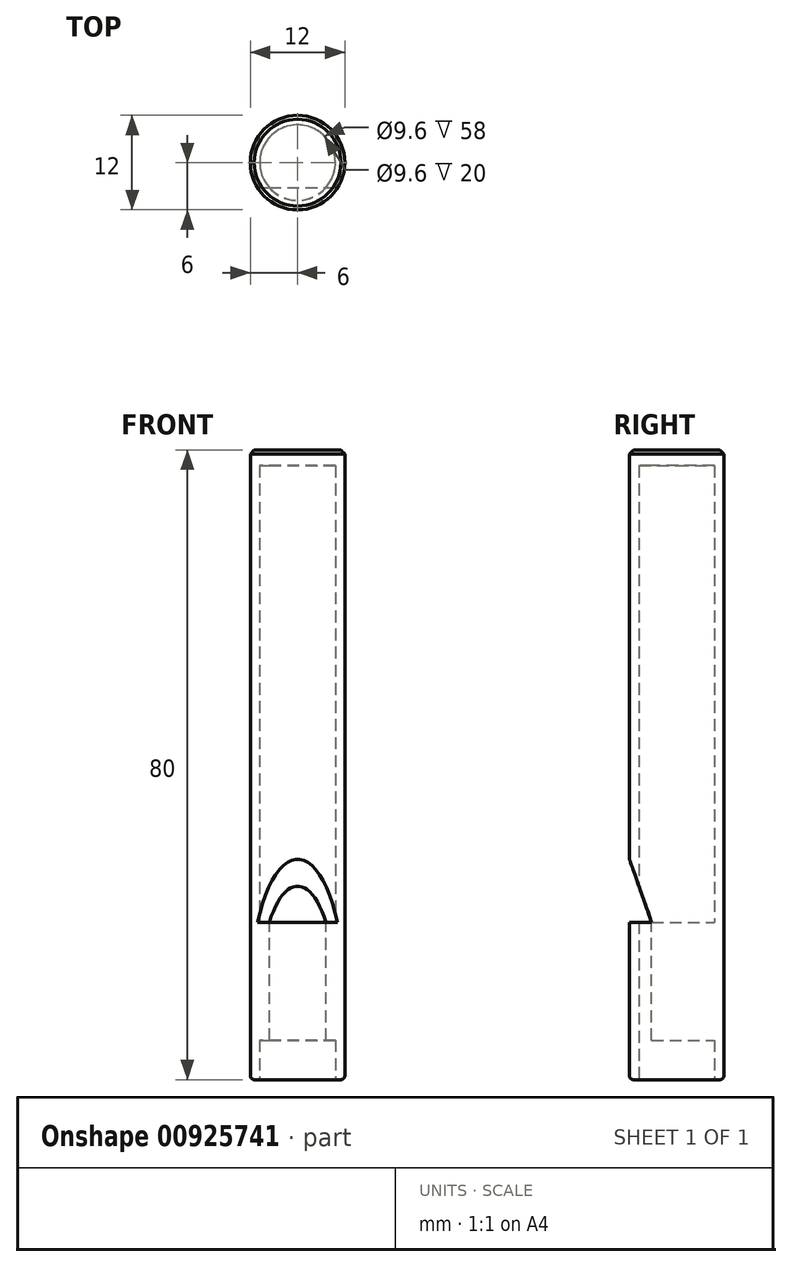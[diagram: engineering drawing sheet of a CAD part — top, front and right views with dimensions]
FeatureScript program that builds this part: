
annotation { "Feature Type Name" : "Feature", "Feature Type Description" : "" }
export const myFeature = defineFeature(function(context is Context, id is Id, definition is map)
    precondition{}
    {
        {
            var Q0;
            Q0=qCreatedBy(makeId("Top.planeOp"),FACE);
            var sketch = newSketch(context, id + "F0", { "sketchPlane" : qUnion([Q0])});
            skCircle(sketch, "E0", {"center": v(0, 0) * mm, "radius": 4.8 * mm});
            skCircle(sketch, "E1", {"center": v(0, 0) * mm, "radius": 6 * mm});
            skSolve(sketch);
        }
        {
            var Q0;
            Q0 = qSketchRegion(id + "F0", true);
            extrude(context, id + "F1", {"entities" : qUnion([Q0]), "depth" : 80 * mm, "offsetDistance" : 25 * mm});
        }
        {
            var Q0;
            Q0=qCreatedBy(makeId("Right.planeOp"),FACE);
            var sketch = newSketch(context, id + "F2", { "sketchPlane" : qUnion([Q0])});
            skLineSegment(sketch, "E2", {"start": v(-6.69, 20) * mm, "end": v(-3.19, 20) * mm});
            skLineSegment(sketch, "E3", {"start": v(-3.19, 20) * mm, "end": v(-6.69, 30) * mm});
            skLineSegment(sketch, "E4", {"start": v(-6.69, 20) * mm, "end": v(-6.69, 30) * mm});
            skSolve(sketch);
        }
        {
            var Q0;
            Q0 = qSketchRegion(id + "F2", true);
            extrude(context, id + "F3", {"entities" : qUnion([Q0]), "operationType" : NewBodyOperationType.REMOVE, "endBound" : BoundingType.SYMMETRIC, "oppositeDirection" : true, "depth" : 25 * mm, "offsetDistance" : 25 * mm});
        }
        {
            var Q0;
            Q0=makeQuery(id+"F3.boolean.opBoolean","COPY",FACE,{"derivedFrom":makeQuery(id+"F3.opExtrude","SWEPT_FACE",FACE,{"disambiguationData":[OSD([sQuery(id+"F2.wireOp",EDGE,"E2")])]})});
            var sketch = newSketch(context, id + "F4", { "sketchPlane" : qUnion([Q0])});
            skArc(sketch, "E5.0", {"start": v(3.59, -3.19) * mm, "mid": v(0, 4.8) * mm, "end": v(-3.59, -3.19) * mm});
            skLineSegment(sketch, "E6", {"start": v(-3.59, -3.19) * mm, "end": v(3.59, -3.19) * mm});
            skSolve(sketch);
        }
        {
            var Q0;
            Q0 = qSketchRegion(id + "F4", true);
            extrude(context, id + "F5", {"entities" : qUnion([Q0]), "operationType" : NewBodyOperationType.ADD, "oppositeDirection" : true, "depth" : 15 * mm, "offsetDistance" : 25 * mm});
        }
        {
            var Q0;
            Q0=makeQuery(id+"F1.opExtrude","CAP_FACE",FACE,{"disambiguationData":[OSD([sQuery(id+"F0.wireOp",EDGE,"E0"),sQuery(id+"F0.wireOp",EDGE,"E1")])],"isStart":false});
            var sketch = newSketch(context, id + "F6", { "sketchPlane" : qUnion([Q0])});
            skCircle(sketch, "E7.0", {"center": v(0, 0) * mm, "radius": 4.8 * mm});
            skSolve(sketch);
        }
        {
            var Q0;
            Q0 = qSketchRegion(id + "F6", true);
            extrude(context, id + "F7", {"entities" : qUnion([Q0]), "operationType" : NewBodyOperationType.ADD, "oppositeDirection" : true, "depth" : 2 * mm, "offsetDistance" : 25 * mm});
        }
        {
            var Q0;
            Q0=makeQuery(id+"F1.opExtrude","CAP_EDGE",EDGE,{"disambiguationData":[OSD([sQuery(id+"F0.wireOp",EDGE,"E1")])],"isStart":true});
            var Q1;
            Q1=makeQuery(id+"Fx6Ps2t5pgFDw5h_1.opExtrude","CAP_EDGE",EDGE,{"disambiguationData":[OSD([sQuery(id+"FsDLp0UN5eIvBDC_1.wireOp",EDGE,"d52d3cf7-acee-48db-a71b-fa19741a61bd")])],"isStart":false});
            fillet(context, id + "F8", {"entities" : qUnion([Q0, Q1]), "radius" : 0.5 * mm, "tangentPropagation" : true, "allowEdgeOverflow" : false});
        }
        {
            var Q0;
            Q0=makeQuery(id+"F1.opExtrude","CAP_EDGE",EDGE,{"disambiguationData":[OSD([sQuery(id+"F0.wireOp",EDGE,"E1")])],"isStart":false});
            chamfer(context, id + "F9", {"entities" : qUnion([Q0]), "width" : 0.5 * mm, "tangentPropagation" : true});
        }
    });
